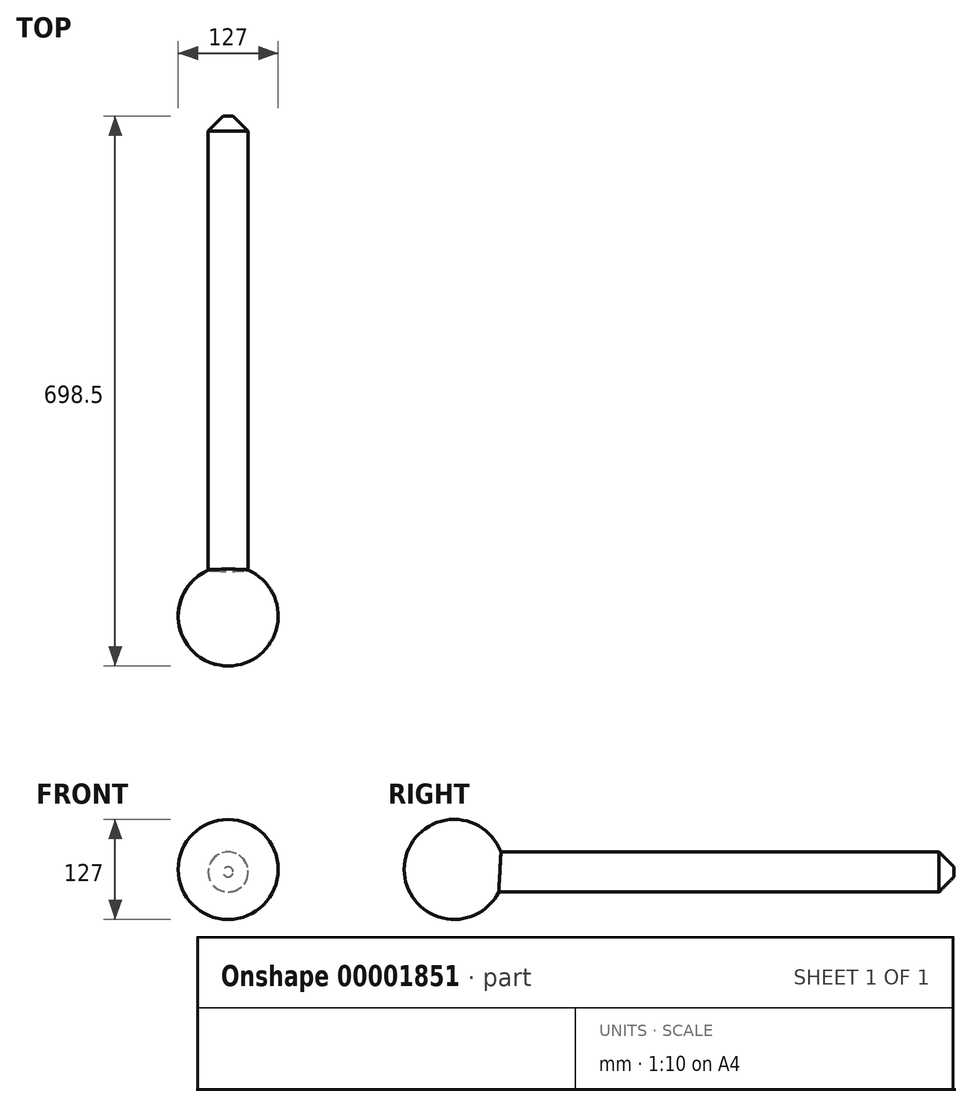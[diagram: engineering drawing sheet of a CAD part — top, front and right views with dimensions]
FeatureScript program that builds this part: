
annotation { "Feature Type Name" : "Feature", "Feature Type Description" : "" }
export const myFeature = defineFeature(function(context is Context, id is Id, definition is map)
    precondition{}
    {
        {
            var Q0;
            Q0=qCreatedBy(makeId("Front.planeOp"),FACE);
            var sketch = newSketch(context, id + "F0", { "sketchPlane" : qUnion([Q0])});
            skCircle(sketch, "E0", {"center": v(0, -3.2) * mm, "radius": 25.4 * mm});
            skSolve(sketch);
        }
        {
            var Q0;
            Q0 = qSketchRegion(id + "F0", true);
            extrude(context, id + "F1", {"entities" : qUnion([Q0]), "endBound" : BoundingType.SYMMETRIC, "depth" : 635 * mm});
        }
        {
            var Q0;
            Q0=makeQuery(id+"F1.opExtrude","CAP_EDGE",EDGE,{"disambiguationData":[OSD([sQuery(id+"F0.wireOp",EDGE,"E0")])],"isStart":false});
            var Q1;
            Q1=makeQuery(id+"F1.opExtrude","CAP_EDGE",EDGE,{"disambiguationData":[OSD([sQuery(id+"F0.wireOp",EDGE,"E0")])],"isStart":true});
            chamfer(context, id + "F2", {"entities" : qUnion([Q0, Q1]), "width" : 19.05 * mm, "tangentPropagation" : true});
        }
        {
            var Q0;
            Q0=qCreatedBy(makeId("Top.planeOp"),FACE);
            var sketch = newSketch(context, id + "F3", { "sketchPlane" : qUnion([Q0])});
            skArc(sketch, "E1", {"start": v(0, -381) * mm, "mid": v(63.5, -317.5) * mm, "end": v(0, -254) * mm});
            skLineSegment(sketch, "E2", {"start": v(0, -381) * mm, "end": v(0, -254) * mm});
            skSolve(sketch);
        }
        {
            var Q0;
            Q0=qCreatedBy(makeId("Top.planeOp"),FACE);
            var sketch = newSketch(context, id + "F4", { "sketchPlane" : qUnion([Q0])});
            skLineSegment(sketch, "E3", {"start": v(0, 0) * mm, "end": v(0, -172.49) * mm, "construction": true});
            skSolve(sketch);
        }
        {
            var Q0;
            Q0=makeQuery(id+"F3.imprint","IMPRINT",FACE,{"disambiguationData":[TD([[makeQuery(id+"F3.imprint","IMPRINT",EDGE,{"derivedFrom":sQuery(id+"F3.wireOp",EDGE,"E1")}),1.0]])]});
            var Q1;
            Q1=sQuery(id+"F4.wireOp",EDGE,"E3");
            revolve(context, id + "F5", {"operationType" : NewBodyOperationType.ADD, "entities" : qUnion([Q0]), "axis" : qUnion([Q1]), "revolveType" : RevolveType.FULL});
        }
    });
